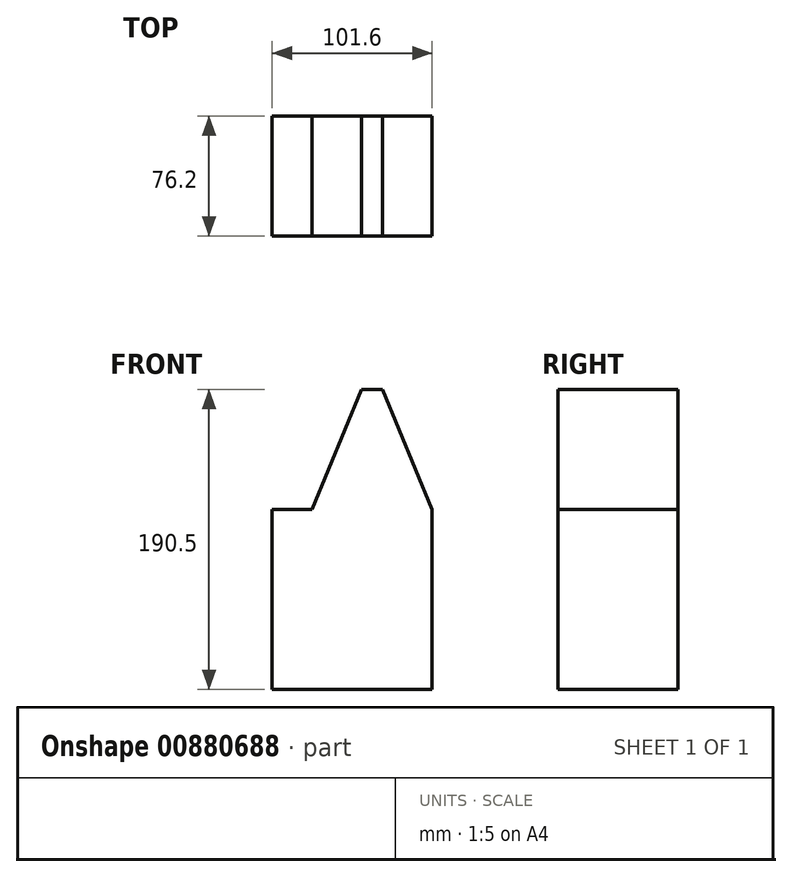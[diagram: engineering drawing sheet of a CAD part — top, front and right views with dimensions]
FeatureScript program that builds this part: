
annotation { "Feature Type Name" : "Feature", "Feature Type Description" : "" }
export const myFeature = defineFeature(function(context is Context, id is Id, definition is map)
    precondition{}
    {
        {
            var Q0;
            Q0=qCreatedBy(makeId("Front.planeOp"),FACE);
            var sketch = newSketch(context, id + "F0", { "sketchPlane" : qUnion([Q0])});
            skLineSegment(sketch, "E0", {"start": v(0, 113.13) * mm, "end": v(-6.83, 113.13) * mm});
            skLineSegment(sketch, "E1", {"start": v(0, 113.13) * mm, "end": v(6.54, 113.13) * mm});
            skLineSegment(sketch, "E2", {"start": v(-6.83, 113.13) * mm, "end": v(6.54, 113.13) * mm});
            skLineSegment(sketch, "E3", {"start": v(-38.1, -77.37) * mm, "end": v(38.1, -77.37) * mm});
            skLineSegment(sketch, "E4", {"start": v(-38.1, -77.37) * mm, "end": v(-38.1, 36.93) * mm});
            skLineSegment(sketch, "E5", {"start": v(38.1, -77.37) * mm, "end": v(38.1, 36.93) * mm});
            skLineSegment(sketch, "E6", {"start": v(-38.1, 36.93) * mm, "end": v(-6.83, 113.13) * mm});
            skLineSegment(sketch, "E7", {"start": v(38.1, 36.93) * mm, "end": v(6.54, 113.13) * mm});
            skLineSegment(sketch, "E8", {"start": v(-38.1, 36.93) * mm, "end": v(38.1, 36.93) * mm});
            skLineSegment(sketch, "E9", {"start": v(0, -77.37) * mm, "end": v(0, 36.93) * mm});
            skLineSegment(sketch, "E10", {"start": v(-19.05, 36.93) * mm, "end": v(-19.05, -77.37) * mm});
            skLineSegment(sketch, "E11", {"start": v(-28.58, 36.93) * mm, "end": v(-28.57, -77.37) * mm});
            skLineSegment(sketch, "E12", {"start": v(-9.53, 36.93) * mm, "end": v(-9.52, -77.37) * mm});
            skLineSegment(sketch, "E13", {"start": v(19.05, 36.93) * mm, "end": v(19.05, -77.37) * mm});
            skLineSegment(sketch, "E14", {"start": v(9.52, 36.93) * mm, "end": v(9.53, -77.37) * mm});
            skLineSegment(sketch, "E15", {"start": v(28.57, 36.93) * mm, "end": v(28.58, -77.37) * mm});
            skSolve(sketch);
        }
        {
            var Q0;
            Q0 = qSketchRegion(id + "F0", true);
            extrude(context, id + "F1", {"entities" : qUnion([Q0]), "depth" : 76.2 * mm, "offsetDistance" : 25.4 * mm});
        }
        {
            var Q0;
            Q0=makeQuery(id+"F1.opExtrude","SWEPT_FACE",FACE,{"disambiguationData":[OSD([sQuery(id+"F0.wireOp",EDGE,"E2")])]});
            var sketch = newSketch(context, id + "F2", { "sketchPlane" : qUnion([Q0])});
            skLineSegment(sketch, "E16", {"start": v(-3.78, 0) * mm, "end": v(-3.78, -76.2) * mm});
            skLineSegment(sketch, "E17", {"start": v(3.06, 0) * mm, "end": v(3.06, -76.2) * mm});
            skSolve(sketch);
        }
        {
            var Q0;
            Q0 = qSketchRegion(id + "F2", true);
            var Q1;
            Q1=makeQuery(id+"F1.opExtrude","CAP_FACE",FACE,{"disambiguationData":[OSD([sQuery(id+"F0.wireOp",EDGE,"E2"),sQuery(id+"F0.wireOp",EDGE,"E3"),sQuery(id+"F0.wireOp",EDGE,"E4"),sQuery(id+"F0.wireOp",EDGE,"E5"),sQuery(id+"F0.wireOp",EDGE,"E6"),sQuery(id+"F0.wireOp",EDGE,"E7")])],"isStart":false});
            extrude(context, id + "F3", {"entities" : qUnion([Q0, Q1]), "operationType" : NewBodyOperationType.ADD, "oppositeDirection" : true, "depth" : 26.42 * mm, "offsetDistance" : 25.4 * mm});
        }
        {
            var Q0;
            Q0 = qSketchRegion(id + "F0", true);
            extrude(context, id + "F4", {"entities" : qUnion([Q0]), "operationType" : NewBodyOperationType.ADD, "depth" : 66.3 * mm, "offsetDistance" : 25.4 * mm});
        }
        {
            var Q0;
            Q0=makeQuery(id+"F1.opExtrude","SWEPT_FACE",FACE,{"disambiguationData":[OSD([sQuery(id+"F0.wireOp",EDGE,"E4")])]});
            extrude(context, id + "F5", {"entities" : qUnion([Q0]), "operationType" : NewBodyOperationType.ADD, "depth" : 25.4 * mm, "offsetDistance" : 25.4 * mm});
        }
        {
            var Q0;
            {var subQ0=sQuery(id+"F0.wireOp",EDGE,"E4");Q0=makeQuery(id+"F5.boolean.opBoolean","MERGE",FACE,{"derivedFrom":[makeQuery(id+"F1.opExtrude","CAP_FACE",FACE,{"disambiguationData":[OSD([sQuery(id+"F0.wireOp",EDGE,"E2"),sQuery(id+"F0.wireOp",EDGE,"E3"),subQ0,sQuery(id+"F0.wireOp",EDGE,"E5"),sQuery(id+"F0.wireOp",EDGE,"E6"),sQuery(id+"F0.wireOp",EDGE,"E7")])],"isStart":true}),makeQuery(id+"F5.opExtrude","SWEPT_FACE",FACE,{"disambiguationData":[OSD([subQ0]),TDD([makeQuery(id+"F1.opExtrude","CAP_EDGE",EDGE,{"disambiguationData":[OSD([subQ0])],"isStart":true})])]})]});}
            extrude(context, id + "F6", {"entities" : qUnion([Q0]), "operationType" : NewBodyOperationType.ADD, "oppositeDirection" : true, "depth" : 22.1 * mm, "offsetDistance" : 25.4 * mm});
        }
    });
